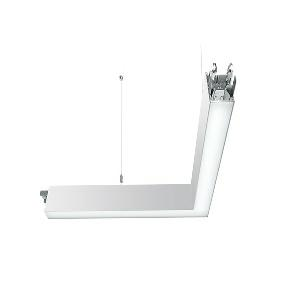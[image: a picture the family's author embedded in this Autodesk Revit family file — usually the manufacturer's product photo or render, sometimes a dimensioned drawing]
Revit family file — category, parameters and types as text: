
# Revit family: idoo_line_-_ilp_3000_vtl_d_ll_mid_00807708_961c
name_source: partatom
category: Lighting Fixtures
units: mm (PartAtom-declared; Revit-internal decimal feet)

## family parameters
Cut with Voids When Loaded = No
Host = Face
Light Source = No
Part Type = Normal
Room Calculation Point = No
Round Connector Dimension = Use Diameter
Shared = No

## types (1)
- IDOO.line - ILP 3000/VTL/D/LL MID (1 x LED, 3150 lm, 2700-6500K)
    Apparent Load = 32 VA
    Approval mark = CE
    CIE Flux Codes = 66 91 98 40 100
    Color Rendering = 90-100
    Color Temperature = 2700-6500K
    Control Gear = Electronic ballast
    Default Elevation = 1800 mm
    Description = ILP 3000/VTL/D|Suspended luminaire|light source: LED|connected load: 220-240 V, 50/60 Hz|Power consumption: approx. 32 W|standby: approx. 0,25|luminous flux: 3150 lm|luminous efficacy: 98 lm/W|light distribution: Direct/indirect|direct ratio: approx. 40 %|colour temperature: Cold white, ca. 2700-6500 K|color rendering index (CRI): >= 90|chromaticity tolerance:  3 SDCM|System of protection: IP 40|technology: Continuously dimmable|luminaire body|material: Sectional aluminium|colour: White|lamp cover: Acrylic (PMMA), Clear|Fastening: Steel cable 0.3 - 0.7 m|glare control: Prism aperture|luminance(L65): <= 2700 cd/m|unified glare rating(4H 8H): <=  16|special features: Specified values at approx. 4000 K, DALI Load 1x, Through-wired, up to 18 m on one mains connection, External control required for Dali Device type 8, Flicker-free, Constant luminous flux between 2700 and 6500 K, Constant colour temperature over the whole dimming range, Continous light without dark z, 90░ rerouting on the left side, Suitable as emergency lighting, Mechanical and electrical connection of the individual modules without tools|
    Frequency = 50 Hz
    Height = 110 mm
    Lamp = 1 x LED
    Lamp Light Flux = 3150 lm
    Lamp count = 1
    Length = 600 mm
    Luminous efficacy = 98 lm/W
    Manufacturer = Waldmann
    ModVariant = No
    Model = 00807708
    Mounting Place = Ceiling
    Mounting Type = Pendant
    Number of Poles = 1
    OnlyDefault = Yes
    Power Factor = 1
    Product Name = IDOO.line - ILP 3000/VTL/D/LL MID
    Product group = Suspended luminaire
    ProductGroupID = 9
    Protection Class = Protection class I
    Protection Degree = IP 40
    RLX_Detail_Level = 1
    RLX_Emergency_Light_Flux = 0 lm
    RLX_Emergency_Type = 0
    RLX_Emergency_Type_DB = No
    RlxData = <blob elided: 21301 chars, md5=54d234a4>
    Socket = socket
    Standby Power = 0 W
    System Light Flux = 3150 lm
    System Power = 32 W
    Type Comments = Product without accessories
    Type Image = ilp_dlp_ll_ws.jpg
    URL = http://relux.com
    VarID = ---
    Voltage = 230 V
    Voltage Range = 220-240 V
    Weight = 0.00 kg
    Width = 600 mm

## geometry (parser evidence)
native form markers: Blend x4, Sweep x13
no freeform markers — native parametric forms only
